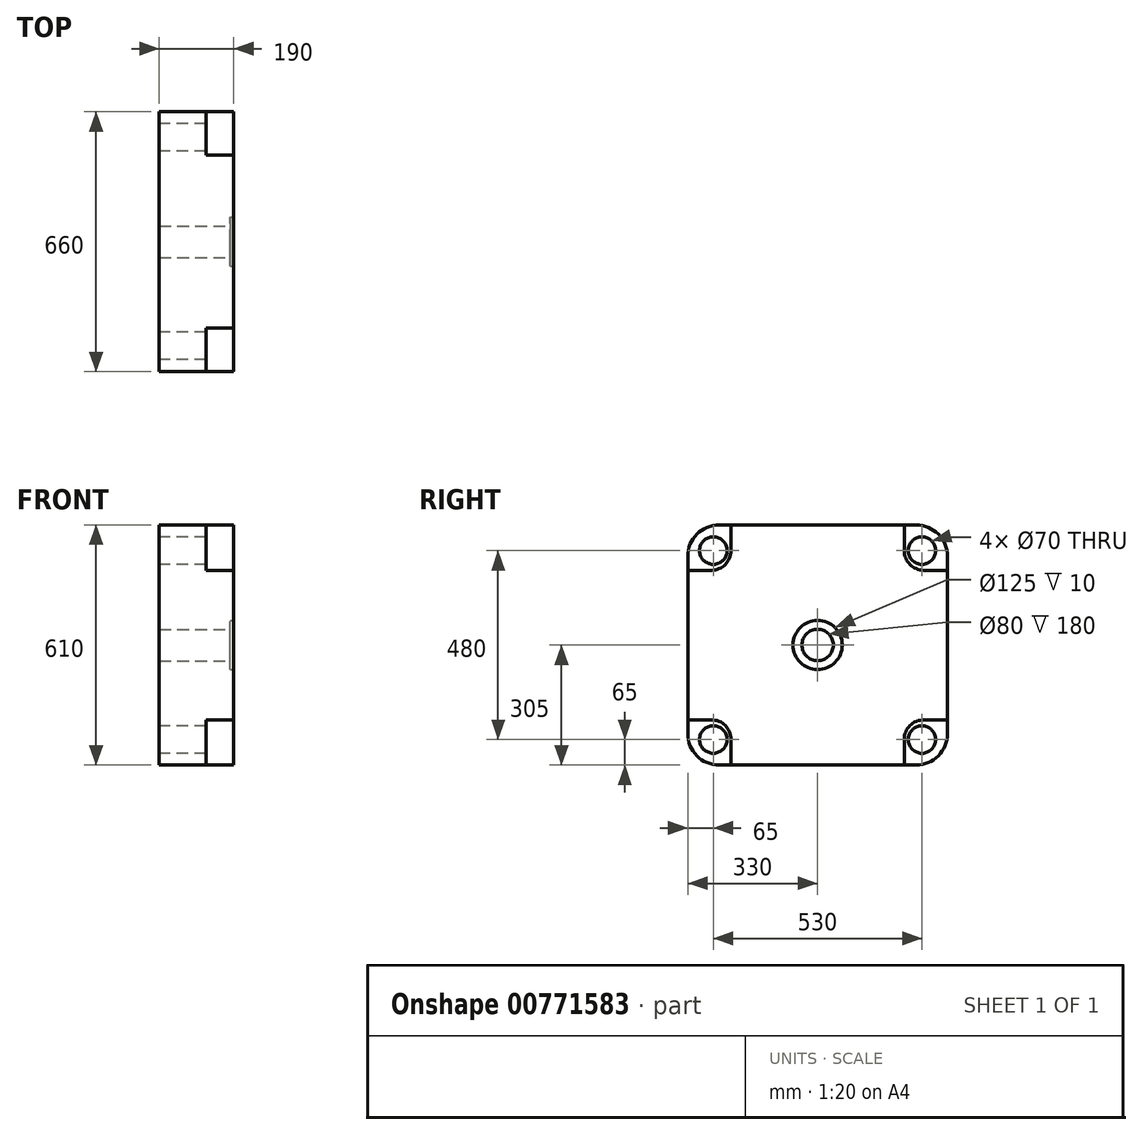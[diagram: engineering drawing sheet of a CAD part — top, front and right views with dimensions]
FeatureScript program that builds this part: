
annotation { "Feature Type Name" : "Feature", "Feature Type Description" : "" }
export const myFeature = defineFeature(function(context is Context, id is Id, definition is map)
    precondition{}
    {
        {
            var Q0;
            Q0=qCreatedBy(makeId("Right.planeOp"),FACE);
            var sketch = newSketch(context, id + "F0", { "sketchPlane" : qUnion([Q0])});
            skLineSegment(sketch, "E0.bottom", {"start": v(330, -305) * mm, "end": v(-330, -305) * mm});
            skLineSegment(sketch, "E0.top", {"start": v(330, 305) * mm, "end": v(-330, 305) * mm});
            skLineSegment(sketch, "E0.left", {"start": v(330, -305) * mm, "end": v(330, 305) * mm});
            skLineSegment(sketch, "E0.right", {"start": v(-330, -305) * mm, "end": v(-330, 305) * mm});
            skPoint(sketch, "E0.middle", {"position": v(0, 0) * mm});
            skSolve(sketch);
        }
        {
            var Q0;
            Q0=makeQuery(id+"F0.imprint","IMPRINT",FACE,{"disambiguationData":[TD([[makeQuery(id+"F0.imprint","IMPRINT",EDGE,{"derivedFrom":sQuery(id+"F0.wireOp",EDGE,"E0.bottom")}),-1.0]])]});
            extrude(context, id + "F1", {"entities" : qUnion([Q0]), "depth" : 120 * mm, "offsetDistance" : 25 * mm});
        }
        {
            var Q0;
            Q0=makeQuery(id+"F1.opExtrude","SWEPT_EDGE",EDGE,{"disambiguationData":[OSD([sQuery(id+"F0.wireOp",EDGE,"E0.top"),sQuery(id+"F0.wireOp",EDGE,"E0.left")])]});
            var Q1;
            Q1=makeQuery(id+"F1.opExtrude","SWEPT_EDGE",EDGE,{"disambiguationData":[OSD([sQuery(id+"F0.wireOp",EDGE,"E0.top"),sQuery(id+"F0.wireOp",EDGE,"E0.right")])]});
            var Q2;
            Q2=makeQuery(id+"F1.opExtrude","SWEPT_EDGE",EDGE,{"disambiguationData":[OSD([sQuery(id+"F0.wireOp",EDGE,"E0.bottom"),sQuery(id+"F0.wireOp",EDGE,"E0.left")])]});
            var Q3;
            Q3=makeQuery(id+"F1.opExtrude","SWEPT_EDGE",EDGE,{"disambiguationData":[OSD([sQuery(id+"F0.wireOp",EDGE,"E0.bottom"),sQuery(id+"F0.wireOp",EDGE,"E0.right")])]});
            fillet(context, id + "F2", {"entities" : qUnion([Q0, Q1, Q2, Q3]), "radius" : 80 * mm, "tangentPropagation" : true, "allowEdgeOverflow" : false});
        }
        {
            var Q0;
            Q0=makeQuery(id+"F1.opExtrude","CAP_FACE",FACE,{"disambiguationData":[OSD([sQuery(id+"F0.wireOp",EDGE,"E0.bottom"),sQuery(id+"F0.wireOp",EDGE,"E0.top"),sQuery(id+"F0.wireOp",EDGE,"E0.left"),sQuery(id+"F0.wireOp",EDGE,"E0.right")])],"isStart":false});
            var sketch = newSketch(context, id + "F3", { "sketchPlane" : qUnion([Q0])});
            skLineSegment(sketch, "E1.bottom", {"start": v(330, -305) * mm, "end": v(-330, -305) * mm});
            skLineSegment(sketch, "E1.top", {"start": v(330, 305) * mm, "end": v(-330, 305) * mm});
            skLineSegment(sketch, "E1.left", {"start": v(330, -305) * mm, "end": v(330, 305) * mm});
            skLineSegment(sketch, "E1.right", {"start": v(-330, -305) * mm, "end": v(-330, 305) * mm});
            skPoint(sketch, "E1.middle", {"position": v(0, 0) * mm});
            skSolve(sketch);
        }
        {
            var Q0;
            {var subQ1=sQuery(id+"F0.wireOp",EDGE,"E0.left");var subQ2=sQuery(id+"F0.wireOp",EDGE,"E0.top");var subQ3=makeQuery(id+"F2.opFillet","BLEND_EDGE",EDGE,{"blendedFrom":[makeQuery(id+"F1.opExtrude","SWEPT_EDGE",EDGE,{"disambiguationData":[OSD([subQ2,subQ1])]}),makeQuery(id+"F1.opExtrude","CAP_FACE",FACE,{"disambiguationData":[OSD([sQuery(id+"F0.wireOp",EDGE,"E0.bottom"),subQ2,subQ1,sQuery(id+"F0.wireOp",EDGE,"E0.right")])],"isStart":false})],"blendedInto":[makeQuery(id+"F1.opExtrude","CAP_FACE",FACE,{"disambiguationData":[OSD([sQuery(id+"F0.wireOp",EDGE,"E0.bottom"),subQ2,subQ1,sQuery(id+"F0.wireOp",EDGE,"E0.right")])],"isStart":false})]});Q0=makeQuery(id+"F3.imprint","IMPRINT",FACE,{"disambiguationData":[TD([[makeQuery(id+"F3.imprint","IMPRINT",EDGE,{"derivedFrom":subQ3}),-1.0]])]});}
            var Q1;
            {var subQ1=sQuery(id+"F0.wireOp",EDGE,"E0.right");var subQ2=sQuery(id+"F0.wireOp",EDGE,"E0.top");var subQ3=makeQuery(id+"F2.opFillet","BLEND_EDGE",EDGE,{"blendedFrom":[makeQuery(id+"F1.opExtrude","SWEPT_EDGE",EDGE,{"disambiguationData":[OSD([subQ2,subQ1])]}),makeQuery(id+"F1.opExtrude","CAP_FACE",FACE,{"disambiguationData":[OSD([sQuery(id+"F0.wireOp",EDGE,"E0.bottom"),subQ2,sQuery(id+"F0.wireOp",EDGE,"E0.left"),subQ1])],"isStart":false})],"blendedInto":[makeQuery(id+"F1.opExtrude","CAP_FACE",FACE,{"disambiguationData":[OSD([sQuery(id+"F0.wireOp",EDGE,"E0.bottom"),subQ2,sQuery(id+"F0.wireOp",EDGE,"E0.left"),subQ1])],"isStart":false})]});Q1=makeQuery(id+"F3.imprint","IMPRINT",FACE,{"disambiguationData":[TD([[makeQuery(id+"F3.imprint","IMPRINT",EDGE,{"derivedFrom":subQ3}),-1.0]])]});}
            var Q2;
            {var subQ1=sQuery(id+"F0.wireOp",EDGE,"E0.right");var subQ2=sQuery(id+"F0.wireOp",EDGE,"E0.left");var subQ3=sQuery(id+"F0.wireOp",EDGE,"E0.top");var subQ4=sQuery(id+"F0.wireOp",EDGE,"E0.bottom");var subQ5=makeQuery(id+"F1.opExtrude","CAP_FACE",FACE,{"disambiguationData":[OSD([subQ4,subQ3,subQ2,subQ1])],"isStart":false});var subQ11=makeQuery(id+"F2.opFillet","BLEND_EDGE",EDGE,{"blendedFrom":[makeQuery(id+"F1.opExtrude","SWEPT_EDGE",EDGE,{"disambiguationData":[OSD([subQ4,subQ2])]}),subQ5],"blendedInto":[subQ5]});Q2=makeQuery(id+"F3.imprint","IMPRINT",FACE,{"disambiguationData":[TD([[makeQuery(id+"F3.imprint","IMPRINT",EDGE,{"derivedFrom":subQ11}),1.0]])]});}
            var Q3;
            {var subQ1=sQuery(id+"F0.wireOp",EDGE,"E0.left");var subQ2=sQuery(id+"F0.wireOp",EDGE,"E0.bottom");var subQ3=makeQuery(id+"F2.opFillet","BLEND_EDGE",EDGE,{"blendedFrom":[makeQuery(id+"F1.opExtrude","SWEPT_EDGE",EDGE,{"disambiguationData":[OSD([subQ2,subQ1])]}),makeQuery(id+"F1.opExtrude","CAP_FACE",FACE,{"disambiguationData":[OSD([subQ2,sQuery(id+"F0.wireOp",EDGE,"E0.top"),subQ1,sQuery(id+"F0.wireOp",EDGE,"E0.right")])],"isStart":false})],"blendedInto":[makeQuery(id+"F1.opExtrude","CAP_FACE",FACE,{"disambiguationData":[OSD([subQ2,sQuery(id+"F0.wireOp",EDGE,"E0.top"),subQ1,sQuery(id+"F0.wireOp",EDGE,"E0.right")])],"isStart":false})]});Q3=makeQuery(id+"F3.imprint","IMPRINT",FACE,{"disambiguationData":[TD([[makeQuery(id+"F3.imprint","IMPRINT",EDGE,{"derivedFrom":subQ3}),-1.0]])]});}
            var Q4;
            {var subQ1=sQuery(id+"F0.wireOp",EDGE,"E0.right");var subQ2=sQuery(id+"F0.wireOp",EDGE,"E0.bottom");var subQ3=makeQuery(id+"F2.opFillet","BLEND_EDGE",EDGE,{"blendedFrom":[makeQuery(id+"F1.opExtrude","SWEPT_EDGE",EDGE,{"disambiguationData":[OSD([subQ2,subQ1])]}),makeQuery(id+"F1.opExtrude","CAP_FACE",FACE,{"disambiguationData":[OSD([subQ2,sQuery(id+"F0.wireOp",EDGE,"E0.top"),sQuery(id+"F0.wireOp",EDGE,"E0.left"),subQ1])],"isStart":false})],"blendedInto":[makeQuery(id+"F1.opExtrude","CAP_FACE",FACE,{"disambiguationData":[OSD([subQ2,sQuery(id+"F0.wireOp",EDGE,"E0.top"),sQuery(id+"F0.wireOp",EDGE,"E0.left"),subQ1])],"isStart":false})]});Q4=makeQuery(id+"F3.imprint","IMPRINT",FACE,{"disambiguationData":[TD([[makeQuery(id+"F3.imprint","IMPRINT",EDGE,{"derivedFrom":subQ3}),-1.0]])]});}
            extrude(context, id + "F4", {"entities" : qUnion([Q0, Q1, Q2, Q3, Q4]), "operationType" : NewBodyOperationType.ADD, "depth" : 70 * mm, "offsetDistance" : 25 * mm});
        }
        {
            var Q0;
            Q0=makeQuery(id+"F4.opExtrude","CAP_FACE",FACE,{"disambiguationData":[OSD([sQuery(id+"F3.wireOp",EDGE,"E1.bottom"),sQuery(id+"F3.wireOp",EDGE,"E1.top"),sQuery(id+"F3.wireOp",EDGE,"E1.left"),sQuery(id+"F3.wireOp",EDGE,"E1.right")])],"isStart":false});
            var sketch = newSketch(context, id + "F5", { "sketchPlane" : qUnion([Q0])});
            skPoint(sketch, "E2", {"position": v(-220, 190) * mm});
            skLineSegment(sketch, "E3", {"start": v(-220, 240) * mm, "end": v(-220, 305) * mm});
            skLineSegment(sketch, "E4", {"start": v(-270, 190) * mm, "end": v(-330, 190) * mm});
            skArc(sketch, "E5.filletArc", {"start": v(-270, 190) * mm, "mid": v(-234.64, 204.64) * mm, "end": v(-220, 240) * mm});
            skLineSegment(sketch, "E6", {"start": v(0, 305) * mm, "end": v(0, -305) * mm});
            skLineSegment(sketch, "E7.MirrorCS", {"start": v(220, 240) * mm, "end": v(220, 305) * mm});
            skArc(sketch, "E8.MirrorCS", {"start": v(270, 190) * mm, "mid": v(234.64, 204.64) * mm, "end": v(220, 240) * mm});
            skLineSegment(sketch, "E9.MirrorCS", {"start": v(270, 190) * mm, "end": v(330, 190) * mm});
            skLineSegment(sketch, "E10", {"start": v(-330, 0) * mm, "end": v(330, 0) * mm});
            skLineSegment(sketch, "E11.MirrorCS", {"start": v(-220, -240) * mm, "end": v(-220, -305) * mm});
            skArc(sketch, "E12.MirrorCS", {"start": v(-270, -190) * mm, "mid": v(-234.64, -204.64) * mm, "end": v(-220, -240) * mm});
            skLineSegment(sketch, "E13.MirrorCS", {"start": v(-270, -190) * mm, "end": v(-330, -190) * mm});
            skLineSegment(sketch, "E14.MirrorCS", {"start": v(270, -190) * mm, "end": v(330, -190) * mm});
            skArc(sketch, "E15.MirrorCS", {"start": v(270, -190) * mm, "mid": v(234.64, -204.64) * mm, "end": v(220, -240) * mm});
            skLineSegment(sketch, "E16.MirrorCS", {"start": v(220, -240) * mm, "end": v(220, -305) * mm});
            skSolve(sketch);
        }
        {
            var Q0;
            {var subQ3=sQuery(id+"F5.wireOp",EDGE,"E3");Q0=makeQuery(id+"F5.imprint","IMPRINT",FACE,{"disambiguationData":[TD([[makeQuery(id+"F5.imprint","IMPRINT",EDGE,{"derivedFrom":subQ3}),1.0]])]});}
            extrude(context, id + "F6", {"entities" : qUnion([Q0]), "operationType" : NewBodyOperationType.REMOVE, "oppositeDirection" : true, "depth" : 70 * mm, "offsetDistance" : 25 * mm});
        }
        {
            var Q0;
            {var subQ4=sQuery(id+"F5.wireOp",EDGE,"E7.MirrorCS");Q0=makeQuery(id+"F5.imprint","IMPRINT",FACE,{"disambiguationData":[TD([[makeQuery(id+"F5.imprint","IMPRINT",EDGE,{"derivedFrom":subQ4}),-1.0]])]});}
            var Q1;
            {var subQ4=sQuery(id+"F5.wireOp",EDGE,"E14.MirrorCS");Q1=makeQuery(id+"F5.imprint","IMPRINT",FACE,{"disambiguationData":[TD([[makeQuery(id+"F5.imprint","IMPRINT",EDGE,{"derivedFrom":subQ4}),-1.0]])]});}
            var Q2;
            {var subQ3=sQuery(id+"F5.wireOp",EDGE,"E11.MirrorCS");Q2=makeQuery(id+"F5.imprint","IMPRINT",FACE,{"disambiguationData":[TD([[makeQuery(id+"F5.imprint","IMPRINT",EDGE,{"derivedFrom":subQ3}),-1.0]])]});}
            extrude(context, id + "F7", {"entities" : qUnion([Q0, Q1, Q2]), "operationType" : NewBodyOperationType.REMOVE, "oppositeDirection" : true, "depth" : 70 * mm, "offsetDistance" : 25 * mm});
        }
        {
            var Q0;
            Q0=makeQuery(id+"F4.opExtrude","CAP_FACE",FACE,{"disambiguationData":[OSD([sQuery(id+"F3.wireOp",EDGE,"E1.bottom"),sQuery(id+"F3.wireOp",EDGE,"E1.top"),sQuery(id+"F3.wireOp",EDGE,"E1.left"),sQuery(id+"F3.wireOp",EDGE,"E1.right")])],"isStart":false});
            var sketch = newSketch(context, id + "F8", { "sketchPlane" : qUnion([Q0])});
            skCircle(sketch, "E17", {"center": v(0, 0) * mm, "radius": 62.5 * mm});
            skSolve(sketch);
        }
        {
            var Q0;
            Q0=makeQuery(id+"F8.imprint","IMPRINT",FACE,{"disambiguationData":[TD([[makeQuery(id+"F8.imprint","IMPRINT",EDGE,{"derivedFrom":sQuery(id+"F8.wireOp",EDGE,"E17")}),1.0]])]});
            extrude(context, id + "F9", {"entities" : qUnion([Q0]), "operationType" : NewBodyOperationType.REMOVE, "oppositeDirection" : true, "depth" : 10 * mm, "offsetDistance" : 25 * mm});
        }
        {
            var Q0;
            Q0=makeQuery(id+"F9.boolean.opBoolean","COPY",FACE,{"derivedFrom":makeQuery(id+"F9.opExtrude","CAP_FACE",FACE,{"disambiguationData":[OSD([sQuery(id+"F8.wireOp",EDGE,"E17")])],"isStart":false})});
            var sketch = newSketch(context, id + "F10", { "sketchPlane" : qUnion([Q0])});
            skCircle(sketch, "E18", {"center": v(0, 0) * mm, "radius": 40 * mm});
            skSolve(sketch);
        }
        {
            var Q0;
            Q0=makeQuery(id+"F10.imprint","IMPRINT",FACE,{"disambiguationData":[TD([[makeQuery(id+"F10.imprint","IMPRINT",EDGE,{"derivedFrom":sQuery(id+"F10.wireOp",EDGE,"E18")}),1.0]])]});
            extrude(context, id + "F11", {"entities" : qUnion([Q0]), "operationType" : NewBodyOperationType.REMOVE, "endBound" : BoundingType.THROUGH_ALL, "oppositeDirection" : true, "depth" : 25 * mm, "offsetDistance" : 25 * mm});
        }
        {
            var Q0;
            Q0=makeQuery(id+"F1.opExtrude","CAP_FACE",FACE,{"disambiguationData":[OSD([sQuery(id+"F0.wireOp",EDGE,"E0.bottom"),sQuery(id+"F0.wireOp",EDGE,"E0.top"),sQuery(id+"F0.wireOp",EDGE,"E0.left"),sQuery(id+"F0.wireOp",EDGE,"E0.right")])],"isStart":true});
            var sketch = newSketch(context, id + "F12", { "sketchPlane" : qUnion([Q0])});
            skPoint(sketch, "E19", {"position": v(-265, 240) * mm});
            skPoint(sketch, "E20", {"position": v(265, 240) * mm});
            skPoint(sketch, "E21", {"position": v(265, -240) * mm});
            skPoint(sketch, "E22", {"position": v(-265, -240) * mm});
            skCircle(sketch, "E23", {"center": v(-265, 240) * mm, "radius": 35 * mm});
            skCircle(sketch, "E24", {"center": v(265, 240) * mm, "radius": 35 * mm});
            skCircle(sketch, "E25", {"center": v(265, -240) * mm, "radius": 35 * mm});
            skCircle(sketch, "E26", {"center": v(-265, -240) * mm, "radius": 35 * mm});
            skSolve(sketch);
        }
        {
            var Q0;
            Q0=makeQuery(id+"F12.imprint","IMPRINT",FACE,{"disambiguationData":[TD([[makeQuery(id+"F12.imprint","IMPRINT",EDGE,{"derivedFrom":sQuery(id+"F12.wireOp",EDGE,"E23")}),1.0]])]});
            var Q1;
            Q1=makeQuery(id+"F12.imprint","IMPRINT",FACE,{"disambiguationData":[TD([[makeQuery(id+"F12.imprint","IMPRINT",EDGE,{"derivedFrom":sQuery(id+"F12.wireOp",EDGE,"E24")}),1.0]])]});
            var Q2;
            Q2=makeQuery(id+"F12.imprint","IMPRINT",FACE,{"disambiguationData":[TD([[makeQuery(id+"F12.imprint","IMPRINT",EDGE,{"derivedFrom":sQuery(id+"F12.wireOp",EDGE,"E25")}),1.0]])]});
            var Q3;
            Q3=makeQuery(id+"F12.imprint","IMPRINT",FACE,{"disambiguationData":[TD([[makeQuery(id+"F12.imprint","IMPRINT",EDGE,{"derivedFrom":sQuery(id+"F12.wireOp",EDGE,"E26")}),1.0]])]});
            extrude(context, id + "F13", {"entities" : qUnion([Q0, Q1, Q2, Q3]), "operationType" : NewBodyOperationType.REMOVE, "endBound" : BoundingType.THROUGH_ALL, "oppositeDirection" : true, "depth" : 25 * mm, "offsetDistance" : 25 * mm});
        }
    });
